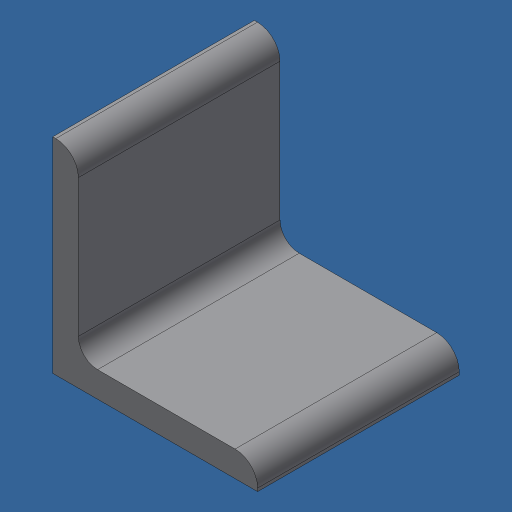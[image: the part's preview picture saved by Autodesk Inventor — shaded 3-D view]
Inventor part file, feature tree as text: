
AUTODESK INVENTOR PART (.ipt)
format: ipt  version: 2024.3 (Build 283343000, 343)  size: 122,880 bytes
history: native  units: mm (DEFAULTED — no unit token found)
features: other x1, extrude x1
ambient origin geometry x8: Origin, YZ Plane, XZ Plane, XY Plane, X Axis, Y Axis, Z Axis, Center Point
bodies: Body1 (feature_tree)
feature tree (2):
  other  "Finish - None"
  extrude  "4" X 4" X 1/2""  Depth=12.7mm
